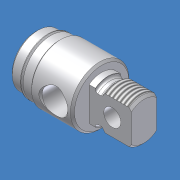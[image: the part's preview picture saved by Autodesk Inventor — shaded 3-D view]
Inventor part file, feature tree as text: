
AUTODESK INVENTOR PART (.ipt)
format: ipt  version: 2012 (Build 160160000, 160)  size: 265,728 bytes
history: native  units: mm (DEFAULTED — no unit token found)
features: other x155, sketch x7, revolve x5, extrude x2, thread x1
ambient origin geometry x8: Origin, YZ Plane, XZ Plane, XY Plane, X Axis, Y Axis, Z Axis, Center Point
bodies: Solid1 (feature_tree)
feature tree (170):
  other  "04P0000_rear_head"
  revolve  "Revolution1"  Angle=360.0deg
  revolve  "Revolution2"  [1 undecoded]
  thread  "Thread1"  [1 undecoded]
  extrude  "Extrusion1"  TaperAngle=360.0deg  [1 undecoded]
  revolve  "Revolution3"  [1 undecoded]
  revolve  "Revolution4"  [1 undecoded]
  revolve  "Revolution5"  [1 undecoded]
  extrude  "Extrusion2"  [1 undecoded]
  other  "c1_XY"
  other  "c1_YZ"
  other  "c1_ZX"
  other  "c1_X"
  other  "c1_Y"
  other  "c1_Z"
  other  "c1_Center"
  other  "cc1_XY"
  other  "cc1_YZ"
  other  "cc1_ZX"
  other  "cc1_X"
  other  "cc1_Y"
  other  "cc1_Z"
  other  "cc1_Center"
  other  "c2_XY"
  other  "c2_YZ"
  other  "c2_ZX"
  other  "c2_X"
  other  "c2_Y"
  other  "c2_Z"
  other  "c2_Center"
  other  "cc2_XY"
  other  "cc2_YZ"
  other  "cc2_ZX"
  other  "cc2_X"
  other  "cc2_Y"
  other  "cc2_Z"
  other  "cc2_Center"
  other  "to_tube_XY"
  other  "to_tube_YZ"
  other  "to_tube_ZX"
  other  "to_tube_X"
  other  "to_tube_Y"
  other  "to_tube_Z"
  other  "to_tube_Center"
  other  "to_nut_XY"
  other  "to_nut_YZ"
  other  "to_nut_ZX"
  other  "to_nut_X"
  other  "to_nut_Y"
  other  "to_nut_Z"
  other  "to_nut_Center"
  other  "lovra1_XY"
  other  "lovra1_YZ"
  other  "lovra1_ZX"
  other  "lovra1_X"
  other  "lovra1_Y"
  other  "lovra1_Z"
  other  "lovra1_Center"
  other  "lovra2_XY"
  other  "lovra2_YZ"
  other  "lovra2_ZX"
  other  "lovra2_X"
  other  "lovra2_Y"
  other  "lovra2_Z"
  other  "lovra2_Center"
  other  "lovra3_XY"
  other  "lovra3_YZ"
  other  "lovra3_ZX"
  other  "lovra3_X"
  other  "lovra3_Y"
  other  "lovra3_Z"
  other  "lovra3_Center"
  other  "to_pin_XY"
  other  "to_pin_YZ"
  other  "to_pin_ZX"
  other  "to_pin_X"
  other  "to_pin_Y"
  other  "to_pin_Z"
  other  "to_pin_Center"
  other  "olen_XY"
  other  "olen_YZ"
  other  "olen_ZX"
  other  "olen_X"
  other  "olen_Y"
  other  "olen_Z"
  other  "olen_Center"
  other  "thd1_XY"
  other  "thd1_YZ"
  other  "thd1_ZX"
  other  "thd1_X"
  other  "thd1_Y"
  other  "thd1_Z"
  other  "thd1_Center"
  other  "p1_XY"
  other  "p1_YZ"
  other  "p1_ZX"
  other  "p1_X"
  other  "p1_Y"
  other  "p1_Z"
  other  "p1_Center"
  other  "thd2_XY"
  other  "thd2_YZ"
  other  "thd2_ZX"
  other  "thd2_X"
  other  "thd2_Y"
  other  "thd2_Z"
  other  "thd2_Center"
  other  "p2_XY"
  other  "p2_YZ"
  other  "p2_ZX"
  other  "p2_X"
  other  "p2_Y"
  other  "p2_Z"
  other  "p2_Center"
  other  "port2_XY"
  other  "port2_YZ"
  other  "port2_ZX"
  other  "port2_X"
  other  "port2_Y"
  other  "port2_Z"
  other  "port2_Center"
  other  "port_XY"
  other  "port_YZ"
  other  "port_ZX"
  other  "port_X"
  other  "port_Y"
  other  "port_Z"
  other  "port_Center"
  other  "1_XY"
  other  "1_YZ"
  other  "1_ZX"
  other  "1_X"
  other  "1_Y"
  other  "1_Z"
  other  "1_Center"
  other  "lovra21_XY"
  other  "lovra21_YZ"
  other  "lovra21_ZX"
  other  "lovra21_X"
  other  "lovra21_Y"
  other  "lovra21_Z"
  other  "lovra21_Center"
  other  "lovra22_XY"
  other  "lovra22_YZ"
  other  "lovra22_ZX"
  other  "lovra22_X"
  other  "lovra22_Y"
  other  "lovra22_Z"
  other  "lovra22_Center"
  other  "to_screw_XY"
  other  "to_screw_YZ"
  other  "to_screw_ZX"
  other  "to_screw_X"
  other  "to_screw_Y"
  other  "to_screw_Z"
  other  "to_screw_Center"
  other  "to_mounting_bracket_XY"
  other  "to_mounting_bracket_YZ"
  other  "to_mounting_bracket_ZX"
  other  "to_mounting_bracket_X"
  other  "to_mounting_bracket_Y"
  other  "to_mounting_bracket_Z"
  other  "to_mounting_bracket_Center"
  sketch  "Sketch_8"  dims[d0=360.0deg d1=360.0deg]
  sketch  "Sketch_15"  dims[d9=14.19225mm d10=0.0mm]
  sketch  "Sketch_9"  dims[d2=9.008135mm d3=0.0mm d4=15.875mm d5=0.0mm d6=360.0deg]
  sketch  "Sketch_13"  dims[d7=360.0deg d8=360.0deg]
  sketch  "Sketch_19"
  sketch  "Sketch_24"
  sketch  "Sketch_43"
note: 7 required parameter values undecoded (feature->parameter linkage not recoverable at this tier; creation-order binding heuristic only, values carry confidence <= 0.55)